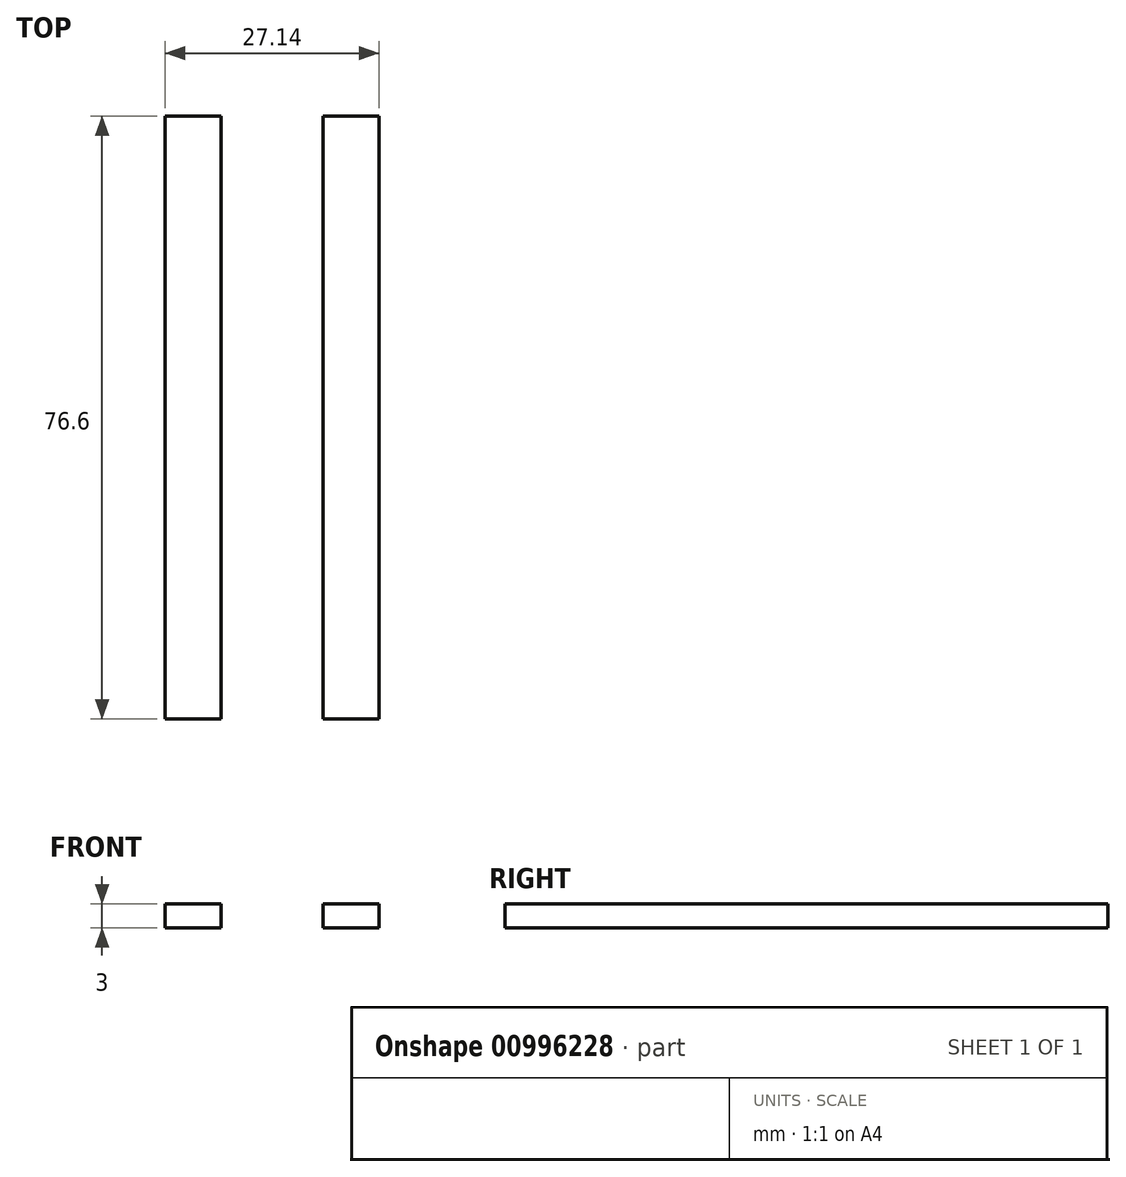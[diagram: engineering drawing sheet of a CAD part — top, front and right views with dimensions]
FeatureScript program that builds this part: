
annotation { "Feature Type Name" : "Feature", "Feature Type Description" : "" }
export const myFeature = defineFeature(function(context is Context, id is Id, definition is map)
    precondition{}
    {
        {
            var Q0;
            Q0=qCreatedBy(makeId("Top.planeOp"),FACE);
            var sketch = newSketch(context, id + "F0", { "sketchPlane" : qUnion([Q0])});
            skLineSegment(sketch, "E0", {"start": v(-13.57, 38.3) * mm, "end": v(-13.57, 0) * mm});
            skLineSegment(sketch, "E1", {"start": v(-13.57, 0) * mm, "end": v(-6.47, 0) * mm});
            skLineSegment(sketch, "E2", {"start": v(-6.47, 0) * mm, "end": v(-6.47, 38.3) * mm});
            skLineSegment(sketch, "E3", {"start": v(-6.47, 38.3) * mm, "end": v(-13.57, 38.3) * mm});
            skLineSegment(sketch, "E4.MirrorCS", {"start": v(13.57, 38.3) * mm, "end": v(13.57, 0) * mm});
            skLineSegment(sketch, "E5.MirrorCS", {"start": v(6.47, 0) * mm, "end": v(6.47, 38.3) * mm});
            skLineSegment(sketch, "E6.MirrorCS", {"start": v(6.47, 38.3) * mm, "end": v(13.57, 38.3) * mm});
            skLineSegment(sketch, "E7.MirrorCS", {"start": v(6.47, 0) * mm, "end": v(6.47, -38.3) * mm});
            skLineSegment(sketch, "E8.MirrorCS", {"start": v(13.57, -38.3) * mm, "end": v(13.57, 0) * mm});
            skLineSegment(sketch, "E9.MirrorCS", {"start": v(6.47, -38.3) * mm, "end": v(13.57, -38.3) * mm});
            skLineSegment(sketch, "E10.MirrorCS", {"start": v(-13.57, -38.3) * mm, "end": v(-13.57, 0) * mm});
            skLineSegment(sketch, "E11.MirrorCS", {"start": v(-6.47, 0) * mm, "end": v(-6.47, -38.3) * mm});
            skLineSegment(sketch, "E12.MirrorCS", {"start": v(-6.47, -38.3) * mm, "end": v(-13.57, -38.3) * mm});
            skSolve(sketch);
        }
        {
            var Q0;
            Q0=makeQuery(id+"F0.imprint","IMPRINT",FACE,{"disambiguationData":[TD([[makeQuery(id+"F0.imprint","IMPRINT",EDGE,{"derivedFrom":sQuery(id+"F0.wireOp",EDGE,"E0")}),1.0]])]});
            var Q1;
            Q1=makeQuery(id+"F0.imprint","IMPRINT",FACE,{"disambiguationData":[TD([[makeQuery(id+"F0.imprint","IMPRINT",EDGE,{"derivedFrom":sQuery(id+"F0.wireOp",EDGE,"E1")}),-1.0]])]});
            var Q2;
            Q2=makeQuery(id+"F0.imprint","IMPRINT",FACE,{"disambiguationData":[TD([[makeQuery(id+"F0.imprint","IMPRINT",EDGE,{"derivedFrom":sQuery(id+"F0.wireOp",EDGE,"E4.MirrorCS")}),-1.0]])]});
            extrude(context, id + "F1", {"entities" : qUnion([Q0, Q1, Q2]), "depth" : 3 * mm, "offsetDistance" : 25 * mm});
        }
    });
